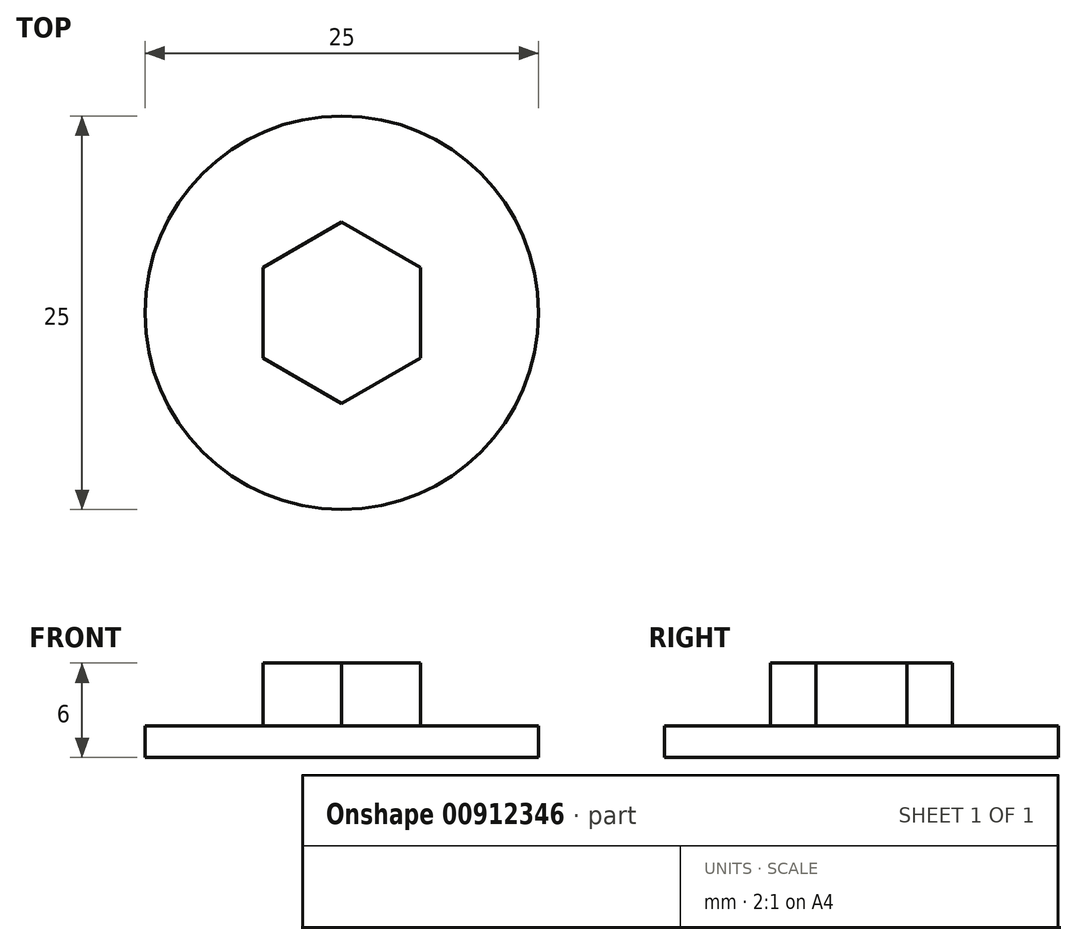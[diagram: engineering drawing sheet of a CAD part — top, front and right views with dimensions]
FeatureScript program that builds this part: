
annotation { "Feature Type Name" : "Feature", "Feature Type Description" : "" }
export const myFeature = defineFeature(function(context is Context, id is Id, definition is map)
    precondition{}
    {
        {
            var Q0;
            Q0=qCreatedBy(makeId("Top.planeOp"),FACE);
            var sketch = newSketch(context, id + "F0", { "sketchPlane" : qUnion([Q0])});
            skCircle(sketch, "E0", {"center": v(0, 0) * mm, "radius": 12.5 * mm});
            skSolve(sketch);
        }
        {
            var Q0;
            Q0=makeQuery(id+"F0.imprint","IMPRINT",FACE,{"disambiguationData":[TD([[makeQuery(id+"F0.imprint","IMPRINT",EDGE,{"derivedFrom":sQuery(id+"F0.wireOp",EDGE,"E0")}),1.0]])]});
            extrude(context, id + "F1", {"entities" : qUnion([Q0]), "oppositeDirection" : true, "depth" : 2 * mm, "offsetDistance" : 25 * mm});
        }
        {
            var Q0;
            Q0=qCreatedBy(makeId("Top.planeOp"),FACE);
            var sketch = newSketch(context, id + "F2", { "sketchPlane" : qUnion([Q0])});
            skCircle(sketch, "E1.cCircle", {"center": v(0, 0) * mm, "radius": 5 * mm, "construction": true});
            skLineSegment(sketch, "E1.0", {"start": v(5, 2.89) * mm, "end": v(5, -2.89) * mm});
            skLineSegment(sketch, "E1.1", {"start": v(5, -2.89) * mm, "end": v(0, -5.77) * mm});
            skLineSegment(sketch, "E1.2", {"start": v(0, -5.77) * mm, "end": v(-5, -2.89) * mm});
            skLineSegment(sketch, "E1.3", {"start": v(-5, -2.89) * mm, "end": v(-5, 2.89) * mm});
            skLineSegment(sketch, "E1.4", {"start": v(-5, 2.89) * mm, "end": v(0, 5.77) * mm});
            skLineSegment(sketch, "E1.5", {"start": v(0, 5.77) * mm, "end": v(5, 2.89) * mm});
            skPoint(sketch, "E1.0.midPoint", {"position": v(5, 0) * mm});
            skSolve(sketch);
        }
        {
            var Q0;
            Q0=makeQuery(id+"F2.imprint","IMPRINT",FACE,{"disambiguationData":[TD([[makeQuery(id+"F2.imprint","IMPRINT",EDGE,{"derivedFrom":sQuery(id+"F2.wireOp",EDGE,"E1.0")}),-1.0]])]});
            extrude(context, id + "F3", {"entities" : qUnion([Q0]), "operationType" : NewBodyOperationType.ADD, "depth" : 4 * mm, "offsetDistance" : 25 * mm});
        }
    });
